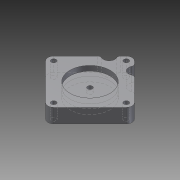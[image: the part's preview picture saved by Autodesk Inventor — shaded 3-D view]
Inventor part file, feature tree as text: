
AUTODESK INVENTOR PART (.ipt)
format: ipt  version: 2011 SP2 (Build 150309200, 309)  size: 140,288 bytes
history: native  units: mm
features: sketch x3, extrude x3, hole x1, fillet x1
ambient origin geometry x8: Origin, YZ Plane, XZ Plane, XY Plane, X Axis, Y Axis, Z Axis, Center Point
bodies: Solid1 (feature_tree)
feature tree (8):
  sketch  "Sketch1"  dims[d0=4.0mm d1=4.0mm]
  extrude  "Extrusion1"  Depth=4.0mm
  extrude  "Extrusion2"  Depth=10.0mm TaperAngle=0.0deg
  hole  "Hole1"  [1 undecoded]
  extrude  "Extrusion3"  Depth=4.0mm
  fillet  "Fillet1"  Radius=3.0mm
  sketch  "Sketch2"  dims[d2=25.4mm d6=10.0mm d14=0.0mm]
  sketch  "Sketch3"  dims[d15=3.4mm d16=6.0mm d17=6.3mm d18=3.0mm d19=90.0deg d20=8.0mm d21=20.594885mm d22=20.05264mm d23=4.0mm d24=3.0mm d25=0.0mm d26=8.5mm d27=8.0mm d28=10.0mm d29=0.0mm d30=2.0mm]
note: 1 required parameter value undecoded (feature->parameter linkage not recoverable at this tier; creation-order binding heuristic only, values carry confidence <= 0.55)
